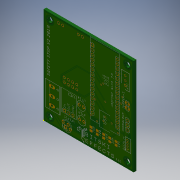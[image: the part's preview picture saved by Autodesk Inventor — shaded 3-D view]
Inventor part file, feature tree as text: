
AUTODESK INVENTOR PART (.ipt)
format: ipt  version: 2019 (Build 230136000, 136)  size: 490,496 bytes
history: native  units: in
note: dims shown in document units (in); Inventor stores cm internally (conversion verified against a paired STEP export)
features: other x3, sketch x2
ambient origin geometry x8: Origin, YZ Plane, XZ Plane, XY Plane, X Axis, Y Axis, Z Axis, Center Point
bodies: Solid1 (feature_tree)
feature tree (5):
  other  "estop v2.brd_Outline"
  sketch  "Sketch2"
  other  "Decal1"
  sketch  "Sketch1"  dims[d0=0.0645in d1=0.0in]
  other  "Image1"
